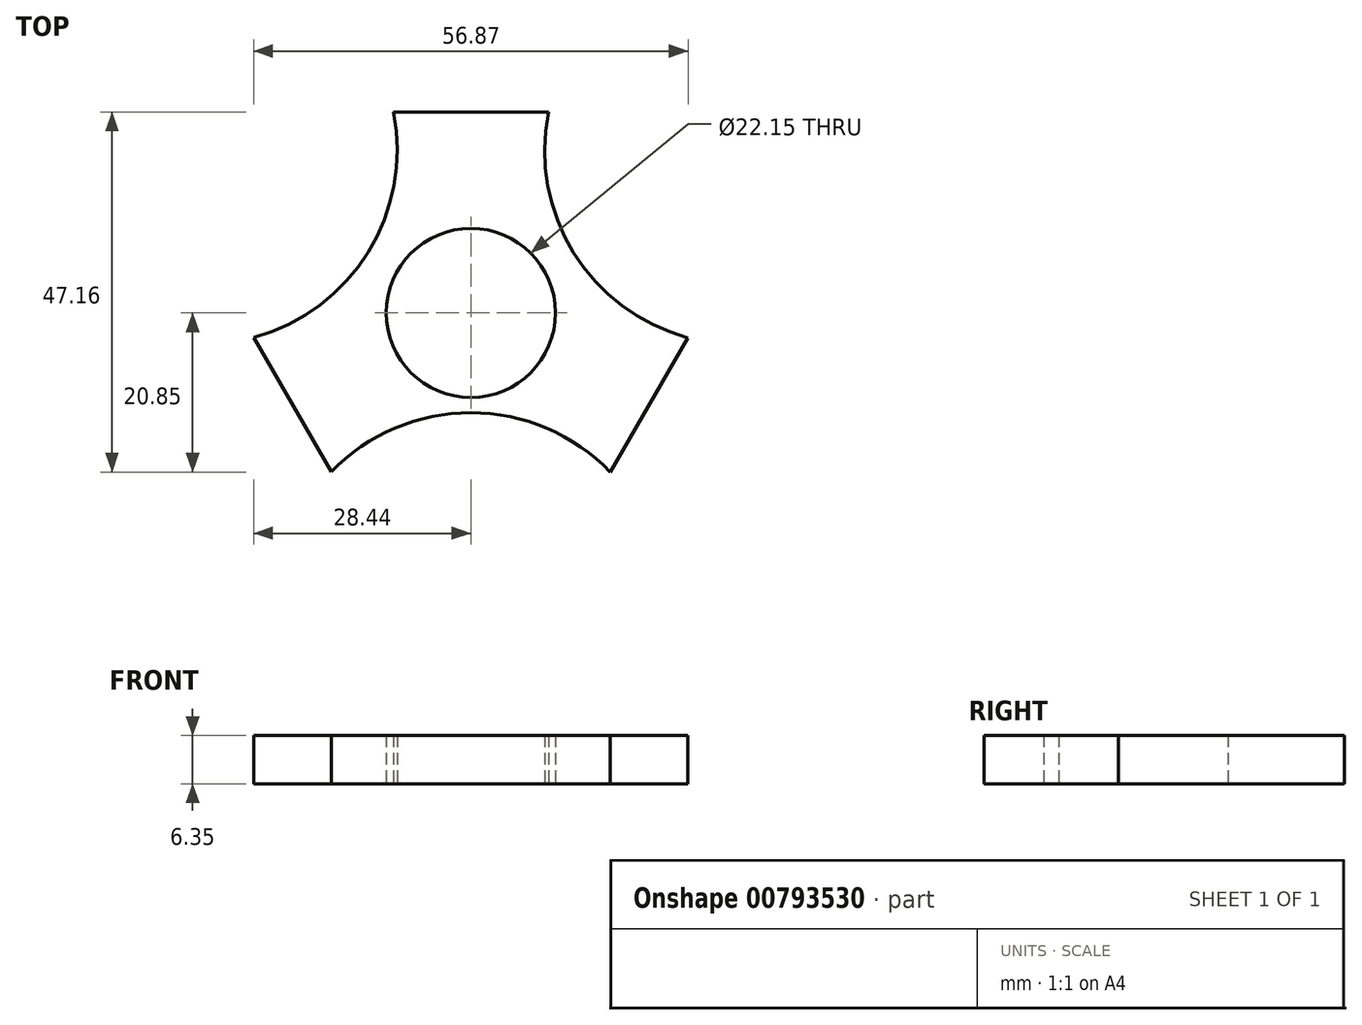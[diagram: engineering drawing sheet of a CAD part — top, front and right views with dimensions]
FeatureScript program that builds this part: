
annotation { "Feature Type Name" : "Feature", "Feature Type Description" : "" }
export const myFeature = defineFeature(function(context is Context, id is Id, definition is map)
    precondition{}
    {
        {
            var Q0;
            Q0=qCreatedBy(makeId("Top.planeOp"),FACE);
            var sketch = newSketch(context, id + "F0", { "sketchPlane" : qUnion([Q0])});
            skCircle(sketch, "E0", {"center": v(0, 0) * mm, "radius": 11.07 * mm});
            skLineSegment(sketch, "E1", {"start": v(0, 11.07) * mm, "end": v(0, 26.31) * mm});
            skLineSegment(sketch, "E2", {"start": v(-10.16, -4.4) * mm, "end": v(-23.36, -12.03) * mm});
            skLineSegment(sketch, "E3", {"start": v(10.15, -4.43) * mm, "end": v(23.35, -12.05) * mm});
            skLineSegment(sketch, "E4", {"start": v(0, 26.31) * mm, "end": v(10.15, 26.31) * mm});
            skLineSegment(sketch, "E5", {"start": v(10.15, 26.31) * mm, "end": v(0, 26.31) * mm});
            skLineSegment(sketch, "E6", {"start": v(0, 26.31) * mm, "end": v(-10.16, 26.31) * mm});
            skLineSegment(sketch, "E7", {"start": v(-23.36, -12.03) * mm, "end": v(-28.44, -3.23) * mm});
            skLineSegment(sketch, "E8", {"start": v(-23.36, -12.03) * mm, "end": v(-18.28, -20.83) * mm});
            skLineSegment(sketch, "E9", {"start": v(23.35, -12.05) * mm, "end": v(28.43, -3.25) * mm});
            skLineSegment(sketch, "E10", {"start": v(28.43, -3.25) * mm, "end": v(23.35, -12.05) * mm});
            skLineSegment(sketch, "E11", {"start": v(23.35, -12.05) * mm, "end": v(18.27, -20.85) * mm});
            skArc(sketch, "E12", {"start": v(-28.44, -3.23) * mm, "mid": v(-13.46, 7.93) * mm, "end": v(-10.16, 26.31) * mm});
            skArc(sketch, "E13", {"start": v(10.15, 26.31) * mm, "mid": v(13.44, 7.91) * mm, "end": v(28.43, -3.25) * mm});
            skArc(sketch, "E14", {"start": v(18.27, -20.85) * mm, "mid": v(0, -13.08) * mm, "end": v(-18.28, -20.83) * mm});
            skSolve(sketch);
        }
        {
            var Q0;
            {var subQ1=sQuery(id+"F0.wireOp",EDGE,"E1");Q0=makeQuery(id+"F0.imprint","IMPRINT",FACE,{"disambiguationData":[TD([[makeQuery(id+"F0.imprint","IMPRINT",EDGE,{"derivedFrom":subQ1}),1.0]])]});}
            var Q1;
            {var subQ0=sQuery(id+"F0.wireOp",EDGE,"E0");var subQ1=makeQuery(id+"F0.imprint","INTERSECT",VERTEX,{"derivedFrom":[subQ0,sQuery(id+"F0.wireOp",EDGE,"E1")]});Q1=makeQuery(id+"F0.imprint","IMPRINT",FACE,{"disambiguationData":[TD([[makeQuery(id+"F0.imprint","IMPRINT",EDGE,{"disambiguationData":[TD([[subQ1,-1.0]])],"derivedFrom":subQ0}),1.0]])]});}
            var Q2;
            {var subQ1=sQuery(id+"F0.wireOp",EDGE,"E1");Q2=makeQuery(id+"F0.imprint","IMPRINT",FACE,{"disambiguationData":[TD([[makeQuery(id+"F0.imprint","IMPRINT",EDGE,{"derivedFrom":subQ1}),-1.0]])]});}
            var Q3;
            {var subQ1=sQuery(id+"F0.wireOp",EDGE,"E2");Q3=makeQuery(id+"F0.imprint","IMPRINT",FACE,{"disambiguationData":[TD([[makeQuery(id+"F0.imprint","IMPRINT",EDGE,{"derivedFrom":subQ1}),1.0]])]});}
            extrude(context, id + "F1", {"entities" : qUnion([Q0, Q1, Q2, Q3]), "depth" : 6.35 * mm, "offsetDistance" : 25.4 * mm});
        }
        {
            var Q0;
            {var subQ0=sQuery(id+"F0.wireOp",EDGE,"E0");var subQ1=makeQuery(id+"F0.imprint","INTERSECT",VERTEX,{"derivedFrom":[subQ0,sQuery(id+"F0.wireOp",EDGE,"E1")]});Q0=makeQuery(id+"F0.imprint","IMPRINT",FACE,{"disambiguationData":[TD([[makeQuery(id+"F0.imprint","IMPRINT",EDGE,{"disambiguationData":[TD([[subQ1,-1.0]])],"derivedFrom":subQ0}),1.0]])]});}
            extrude(context, id + "F2", {"entities" : qUnion([Q0]), "operationType" : NewBodyOperationType.REMOVE, "oppositeDirection" : true, "depth" : -914.4 * mm, "offsetDistance" : 25.4 * mm});
        }
    });
